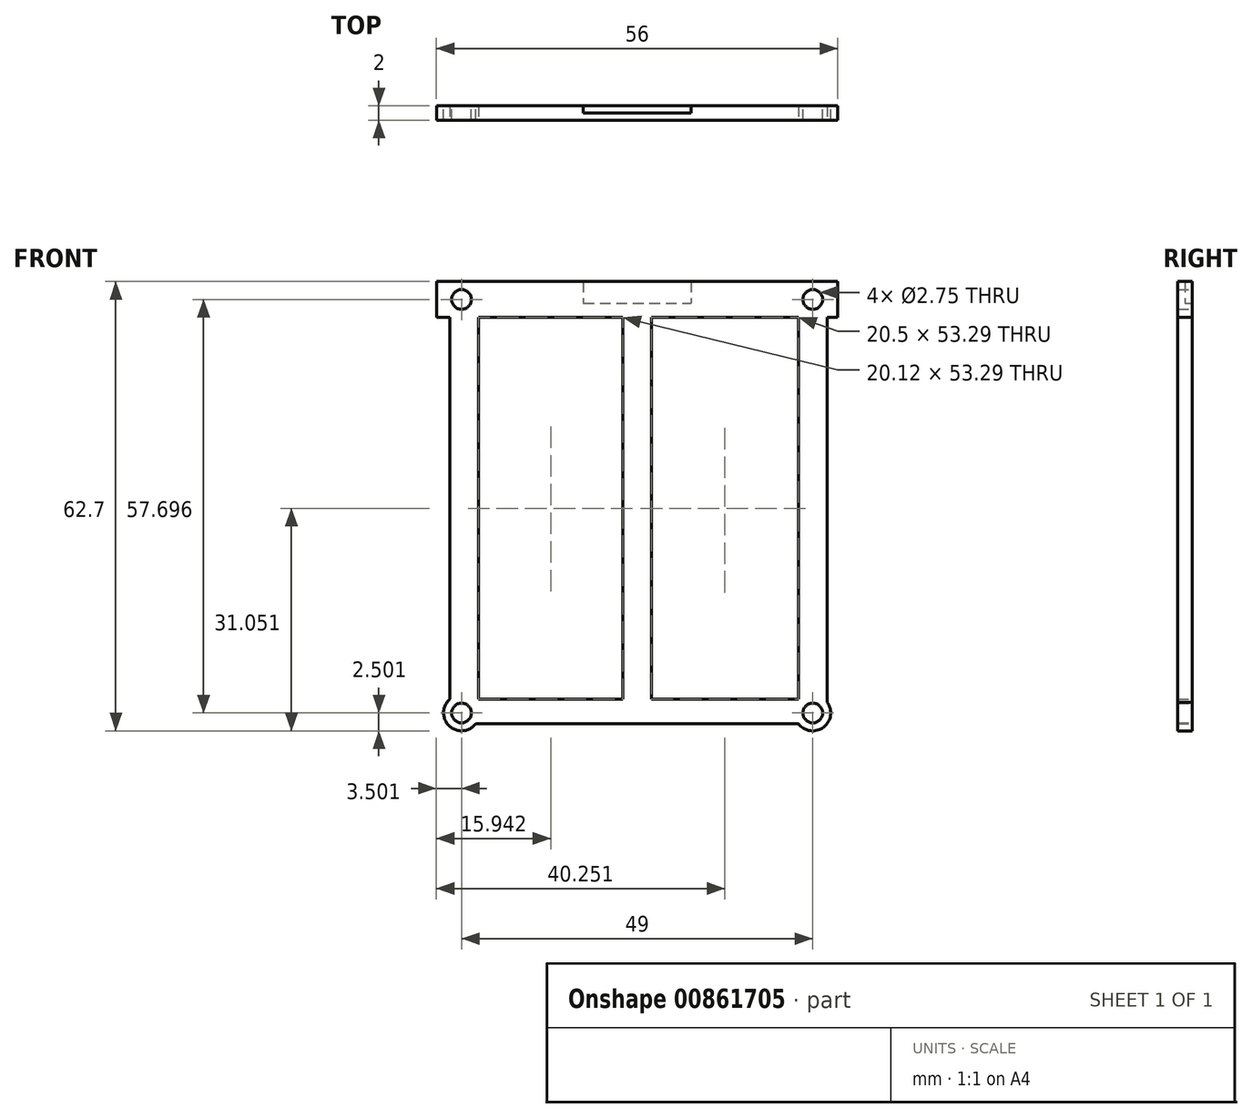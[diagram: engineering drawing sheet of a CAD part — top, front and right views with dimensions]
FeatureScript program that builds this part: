
annotation { "Feature Type Name" : "Feature", "Feature Type Description" : "" }
export const myFeature = defineFeature(function(context is Context, id is Id, definition is map)
    precondition{}
    {
        {
            var Q0;
            Q0=qCreatedBy(makeId("Front.planeOp"),FACE);
            var sketch = newSketch(context, id + "F0", { "sketchPlane" : qUnion([Q0])});
            skLineSegment(sketch, "E0.bottom", {"start": v(-6.75, 18.4) * mm, "end": v(8.25, 18.4) * mm});
            skLineSegment(sketch, "E0.top", {"start": v(-6.75, 15.4) * mm, "end": v(8.25, 15.4) * mm});
            skLineSegment(sketch, "E0.left", {"start": v(-6.75, 18.4) * mm, "end": v(-6.75, 15.4) * mm});
            skLineSegment(sketch, "E0.right", {"start": v(8.25, 18.4) * mm, "end": v(8.25, 15.4) * mm});
            skPoint(sketch, "E1.center.orphan", {"position": v(-6.75, 16.9) * mm});
            skPoint(sketch, "E2.center.orphan", {"position": v(8.25, 16.9) * mm});
            skSolve(sketch);
        }
        {
            var Q0;
            Q0=qCreatedBy(makeId("Front.planeOp"),FACE);
            var sketch = newSketch(context, id + "F1", { "sketchPlane" : qUnion([Q0])});
            skLineSegment(sketch, "E3.bottom", {"start": v(-27.25, 18.4) * mm, "end": v(28.75, 18.4) * mm});
            skLineSegment(sketch, "E3.top", {"start": v(-27.25, 13.4) * mm, "end": v(28.75, 13.4) * mm});
            skLineSegment(sketch, "E3.left", {"start": v(-27.25, 18.4) * mm, "end": v(-27.25, 13.4) * mm});
            skLineSegment(sketch, "E3.right", {"start": v(28.75, 18.4) * mm, "end": v(28.75, 13.4) * mm});
            skLineSegment(sketch, "E4.bottom", {"start": v(-22.37, 15.9) * mm, "end": v(23.88, 15.9) * mm, "construction": true});
            skLineSegment(sketch, "E4.top", {"start": v(-23.75, -43.47) * mm, "end": v(25.25, -43.47) * mm, "construction": true});
            skLineSegment(sketch, "E4.left", {"start": v(-23.75, 14.53) * mm, "end": v(-23.75, -43.47) * mm, "construction": true});
            skLineSegment(sketch, "E4.right", {"start": v(25.25, 14.53) * mm, "end": v(25.25, -43.47) * mm, "construction": true});
            skLineSegment(sketch, "E5", {"start": v(-25.12, 15.9) * mm, "end": v(-23.14, 15.9) * mm, "construction": true});
            skCircle(sketch, "E6", {"center": v(-23.75, 15.9) * mm, "radius": 1.38 * mm});
            skCircle(sketch, "E7", {"center": v(25.25, 15.9) * mm, "radius": 1.38 * mm});
            skLineSegment(sketch, "E8.trimOffspring", {"start": v(26.63, 15.9) * mm, "end": v(28.75, 15.9) * mm, "construction": true});
            skSolve(sketch);
        }
        {
            var Q0;
            Q0=qSketchRegion(id+"F1",true);
            extrude(context, id + "F2", {"entities" : qUnion([Q0]), "depth" : 2 * mm, "offsetDistance" : 25 * mm});
        }
        {
            var Q0;
            Q0=qSketchRegion(id+"F0",true);
            extrude(context, id + "F3", {"entities" : qUnion([Q0]), "operationType" : NewBodyOperationType.REMOVE, "depth" : 1 * mm, "offsetDistance" : 25 * mm});
        }
        {
            var Q0;
            Q0=qCreatedBy(makeId("Front.planeOp"),FACE);
            var sketch = newSketch(context, id + "F4", { "sketchPlane" : qUnion([Q0])});
            skLineSegment(sketch, "E9.bottom", {"start": v(-23.75, 15.9) * mm, "end": v(25.25, 15.9) * mm, "construction": true});
            skLineSegment(sketch, "E9.top", {"start": v(-23.75, -41.79) * mm, "end": v(-21.97, -41.79) * mm, "construction": true});
            skLineSegment(sketch, "E9.left", {"start": v(-23.75, 15.9) * mm, "end": v(-23.75, -41.79) * mm, "construction": true});
            skLineSegment(sketch, "E9.right", {"start": v(25.25, 16.21) * mm, "end": v(25.25, -41.79) * mm, "construction": true});
            skLineSegment(sketch, "E10", {"start": v(-17.11, 15.9) * mm, "end": v(74.62, 15.9) * mm, "construction": true});
            skCircle(sketch, "E11", {"center": v(25.25, -41.79) * mm, "radius": 1.38 * mm});
            skCircle(sketch, "E12", {"center": v(-23.75, -41.79) * mm, "radius": 1.38 * mm});
            skCircle(sketch, "E13", {"center": v(-23.75, -41.79) * mm, "radius": 2.5 * mm});
            skCircle(sketch, "E14", {"center": v(25.25, -41.79) * mm, "radius": 2.5 * mm});
            skLineSegment(sketch, "E15.bottom", {"start": v(-25.37, -39.88) * mm, "end": v(-21.37, -39.88) * mm});
            skLineSegment(sketch, "E15.top", {"start": v(-25.37, 13.65) * mm, "end": v(-21.37, 13.65) * mm});
            skLineSegment(sketch, "E15.left", {"start": v(-25.37, -39.88) * mm, "end": v(-25.37, 13.65) * mm});
            skLineSegment(sketch, "E15.right", {"start": v(-21.37, -39.88) * mm, "end": v(-21.37, 9.7) * mm});
            skLineSegment(sketch, "E16.bottom", {"start": v(23.25, -40.29) * mm, "end": v(27.25, -40.29) * mm});
            skLineSegment(sketch, "E16.top", {"start": v(23.25, 13.65) * mm, "end": v(27.25, 13.65) * mm});
            skLineSegment(sketch, "E16.left", {"start": v(23.25, -40.29) * mm, "end": v(23.25, -39.88) * mm});
            skLineSegment(sketch, "E16.right", {"start": v(27.25, -40.29) * mm, "end": v(27.25, 13.65) * mm});
            skLineSegment(sketch, "E17.bottom", {"start": v(-21.37, -39.88) * mm, "end": v(20.26, -39.88) * mm});
            skLineSegment(sketch, "E17.top", {"start": v(-21.37, -43.29) * mm, "end": v(23.25, -43.29) * mm});
            skLineSegment(sketch, "E17.right", {"start": v(23.25, -39.88) * mm, "end": v(23.25, -43.29) * mm});
            skLineSegment(sketch, "E18.trimOffspring", {"start": v(23.25, -35.96) * mm, "end": v(23.25, 13.65) * mm});
            skLineSegment(sketch, "E19.trimOffspring", {"start": v(23.32, -43.38) * mm, "end": v(23.25, -43.29) * mm});
            skLineSegment(sketch, "E20", {"start": v(-21.37, 9.7) * mm, "end": v(-21.37, 13.65) * mm});
            skLineSegment(sketch, "E21", {"start": v(20.26, -39.88) * mm, "end": v(23.25, -39.88) * mm});
            skLineSegment(sketch, "E22", {"start": v(23.25, -35.96) * mm, "end": v(23.25, -39.88) * mm});
            skLineSegment(sketch, "E23.bottom", {"start": v(-1.25, 13.4) * mm, "end": v(2.75, 13.4) * mm});
            skLineSegment(sketch, "E23.top", {"start": v(-1.25, -39.88) * mm, "end": v(2.75, -39.88) * mm});
            skLineSegment(sketch, "E23.left", {"start": v(-1.25, 13.4) * mm, "end": v(-1.25, -39.88) * mm});
            skLineSegment(sketch, "E23.right", {"start": v(2.75, 13.4) * mm, "end": v(2.75, -39.88) * mm});
            skLineSegment(sketch, "E24", {"start": v(-21.37, -43.29) * mm, "end": v(-21.75, -43.29) * mm});
            skLineSegment(sketch, "E25.trimOffspring", {"start": v(-21.37, -41.79) * mm, "end": v(25.25, -41.79) * mm, "construction": true});
            skSolve(sketch);
        }
        {
            var Q0;
            Q0=qSketchRegion(id+"F4",true);
            extrude(context, id + "F5", {"entities" : qUnion([Q0]), "operationType" : NewBodyOperationType.ADD, "depth" : 2 * mm, "offsetDistance" : 25 * mm});
        }
    });
